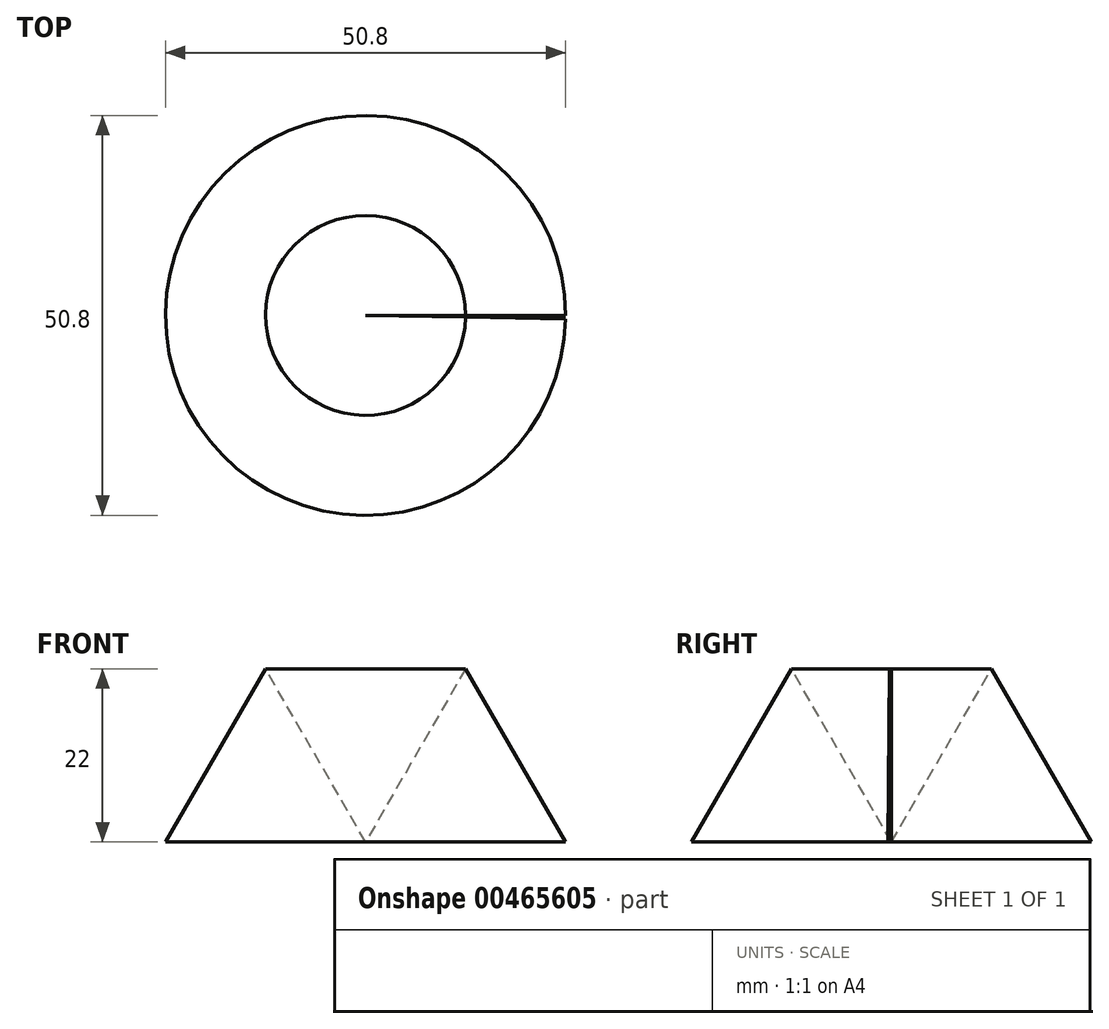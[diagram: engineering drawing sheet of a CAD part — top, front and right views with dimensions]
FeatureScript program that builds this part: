
annotation { "Feature Type Name" : "Feature", "Feature Type Description" : "" }
export const myFeature = defineFeature(function(context is Context, id is Id, definition is map)
    precondition{}
    {
        {
            var Q0;
            Q0=qCreatedBy(makeId("Front.planeOp"),FACE);
            var sketch = newSketch(context, id + "F0", { "sketchPlane" : qUnion([Q0])});
            skLineSegment(sketch, "E0", {"start": v(0, 0) * mm, "end": v(25.4, 0) * mm});
            skLineSegment(sketch, "E1", {"start": v(25.4, 0) * mm, "end": v(12.7, 22) * mm});
            skLineSegment(sketch, "E2", {"start": v(12.7, 22) * mm, "end": v(0, 0) * mm});
            skLineSegment(sketch, "E3", {"start": v(0, 0) * mm, "end": v(0, 47.97) * mm, "construction": true});
            skSolve(sketch);
        }
        {
            var Q0;
            Q0=makeQuery(id+"F0.imprint","IMPRINT",FACE,{"disambiguationData":[TD([[makeQuery(id+"F0.imprint","IMPRINT",EDGE,{"derivedFrom":sQuery(id+"F0.wireOp",EDGE,"E0")}),1.0]])]});
            var Q1;
            Q1=sQuery(id+"F0.wireOp",EDGE,"E3");
            revolve(context, id + "F1", {"entities" : qUnion([Q0]), "axis" : qUnion([Q1]), "revolveType" : RevolveType.ONE_DIRECTION, "angle" : 359 * degree});
        }
    });
